# Revit family: Sofiero-Bar-table-OM
name_source: partatom
category: Furniture
units: mm (PartAtom-declared; Revit-internal decimal feet)

## family parameters
Always vertical = Yes
Cut with Voids When Loaded = No
OmniClass Number = 23.21.23.13.15
Room Calculation Point = No
Shared = No
Work Plane-Based = No

## types (4) — shared parameters
BIMobject category = Tables
Description = Bar table Sofiero Above Ground
Edition number = 1
IFC Classification = Furniture
Manufacturer = Hags
Manufacturer name = HAGS
OmniClass Code = 23-11 29 15
OmniClass Description = Exterior Tables
Product Guid = bb553ecb-7594-4ca6-a00d-3779d998405c
Product SKU = Sofiero_Bar_table_Above_Ground
Product data url = https://bimobject.com
Product name = Sofiero Bar table
QR code = https://bimobject.com
URL = https://www.hags.com
Uniclass 1.4 Code = JN
Uniclass 1.4 Description = Furniture/Equipment
zero-valued in all types: Default Elevation

## per-type parameters (varying)
| type | Body material | Body material_90 | Construction material | Model | Product url |
| 8077436 Bark Brown / Black | Hags - Wood - Bark brown | Hags - Wood - Bark brown 90 | Hags - Steel - Powder coated - Black | 8077436 | https://hags.se |
| 8077439 Tan / Galvanized | Hags - Wood - Tan | Hags - Wood - Tan 90 | Hags - Steel - Galvanized | 8077439 | https://hags.se |
| 8097648 Hardwood / Galvanized | Hags - Hard Wood | Hags - Hard Wood | Hags - Steel - Galvanized | 8097648 | https://www.hags.com |
| 8097649 Hardwood / Black | Hags - Hard Wood | Hags - Hard Wood | Hags - Steel - Powder coated - Black | 8097649 | https://www.hags.com |

## geometry (parser evidence)
native form markers: Sweep x4
no freeform markers — native parametric forms only
